# Revit family: 2101A_HBA_Wasp2
name_source: partatom
category: Communication Devices
units: mm (PartAtom-declared; Revit-internal decimal feet)

## family parameters
Cut with Voids When Loaded = No
Host = Face
Maintain Annotation Orientation = No
OmniClass Number = 23.85.80.11.27
OmniClass Title = Lighting Controls
Part Type = Normal
Room Calculation Point = No
Round Connector Dimension = Use Diameter
Shared = Yes

## types (1)
- 2101A_HBA_Wasp2
    Assembly Code = D5090
    Certifications = Conforms to UL STD 508, UL STD 244A
    Coverage = 360°, 180°, Aisle, Half Aisle
    Default Elevation = 48 "
    Description = The WASP2 Indoor/Outdoor Occupancy Sensor is specifically
designed for On/Off control of high bay fixtures in warehouse,
distribution centers and similar facilities. The WASP2 sensor is also
available for low mount applications when using the appropriate
lens. The sensor is available in end mount and surface mount
versions with either single or dual outputs
    Features = Digital Passive Infrared (PIR) sensor 
	 Supported mounting heights: High mount lens: 30 ft (9.14m) outdoors; 45 ft indoors (13.72m) 
	Low mount lens: 16 ft indoors/outdoors (4.88m) 
	 Multiple (single and dual) output versions 
	 Unique Smart Cycling for improved lamp life 
	 End mount and surface mount versions 
	Interchangeable high/low area detection lens options 
	 Low voltage and line voltage models available 
	 Daylight sensor for daylight harvesting applications 
	 Low temperature/water-tight/indoor-outdoor versions 
	 Withstands low temperature and conforms to IP65 water- tight-standards 
	 UL and cUL listed 
	 Five-year limited warranty
    Housing Material = Paint -  Matte White
    Manufacturer = NX Lighting Controls
    Model = WASP™ 2 Occupancy Sensor
    Power Requirements = Line Voltage sensors: 120/277/347VAC, 208/240VAC, 480VAC, 60 Hz
Low Voltage sensors: 24VDC (uses UVPP or MP-Series power pack – not included)
    Sensing Element = Glass -  White
    Type Comments = Occupancy Sensors and Controllers
    URL = https://www.currentlighting.com
    Warranty = 5-Years Warranty
    Width = 4 "

## geometry (parser evidence)
native form markers: Sweep x3
no freeform markers — native parametric forms only
